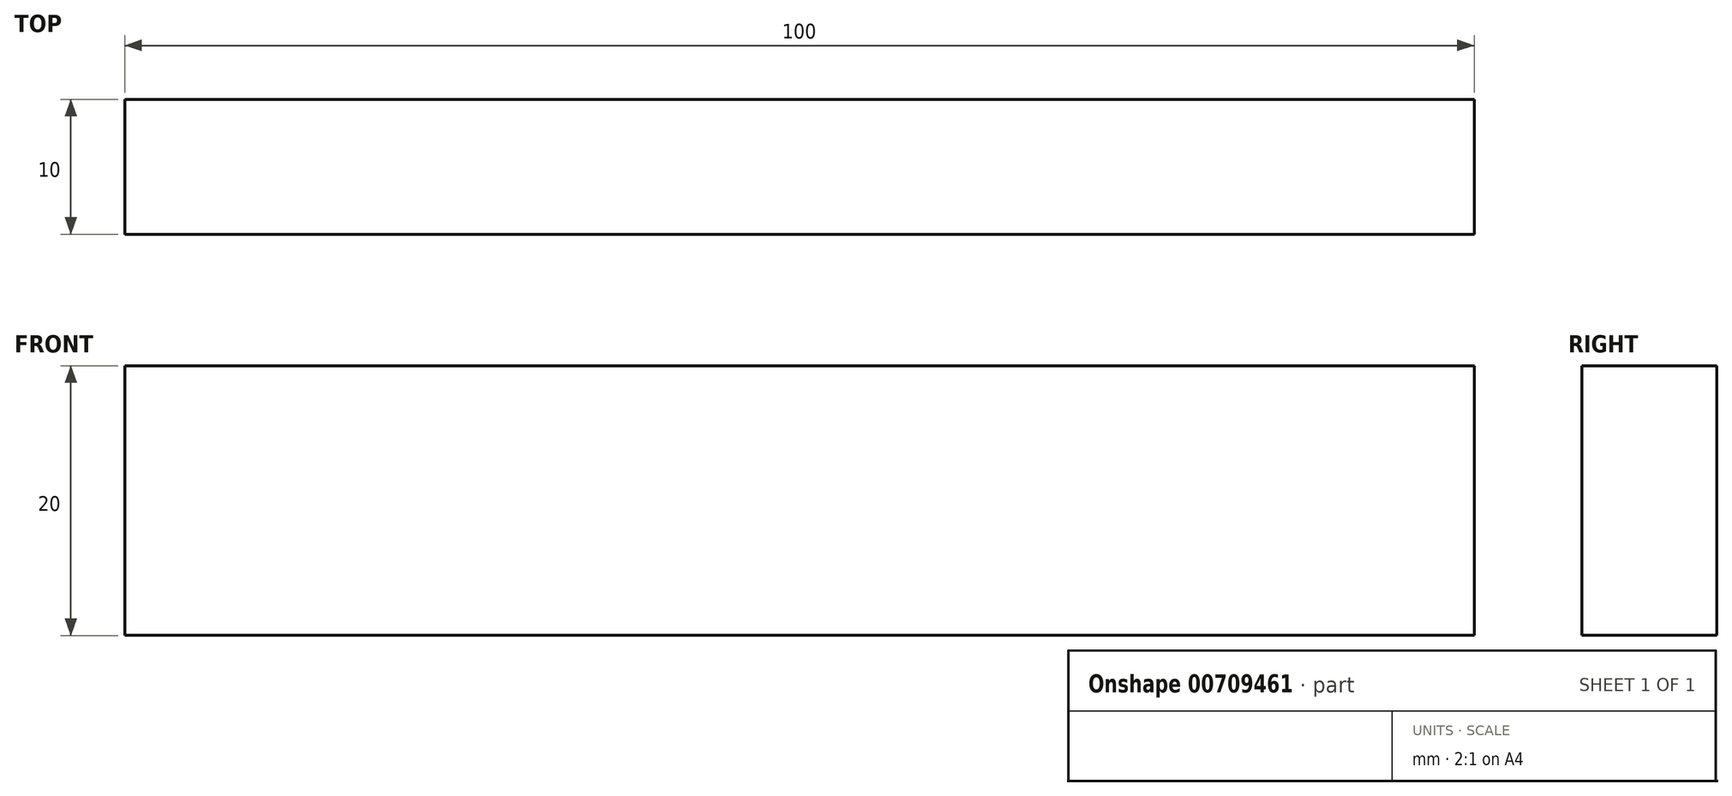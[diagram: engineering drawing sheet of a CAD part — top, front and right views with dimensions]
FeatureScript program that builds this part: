
annotation { "Feature Type Name" : "Feature", "Feature Type Description" : "" }
export const myFeature = defineFeature(function(context is Context, id is Id, definition is map)
    precondition{}
    {
        {
            var Q0;
            Q0=qCreatedBy(makeId("Front.planeOp"),FACE);
            var sketch = newSketch(context, id + "F0", { "sketchPlane" : qUnion([Q0])});
            skLineSegment(sketch, "E0.bottom", {"start": v(-56.22, 27.25) * mm, "end": v(43.78, 27.25) * mm});
            skLineSegment(sketch, "E0.top", {"start": v(-56.22, 7.25) * mm, "end": v(43.78, 7.25) * mm});
            skLineSegment(sketch, "E0.left", {"start": v(-56.22, 27.25) * mm, "end": v(-56.22, 7.25) * mm});
            skLineSegment(sketch, "E0.right", {"start": v(43.78, 27.25) * mm, "end": v(43.78, 7.25) * mm});
            skSolve(sketch);
        }
        {
            var Q0;
            Q0=makeQuery(id+"F0.imprint","IMPRINT",FACE,{"disambiguationData":[TD([[makeQuery(id+"F0.imprint","IMPRINT",EDGE,{"derivedFrom":sQuery(id+"F0.wireOp",EDGE,"E0.bottom")}),-1.0]])]});
            extrude(context, id + "F1", {"entities" : qUnion([Q0]), "depth" : 10 * mm, "offsetDistance" : 25.4 * mm});
        }
    });
